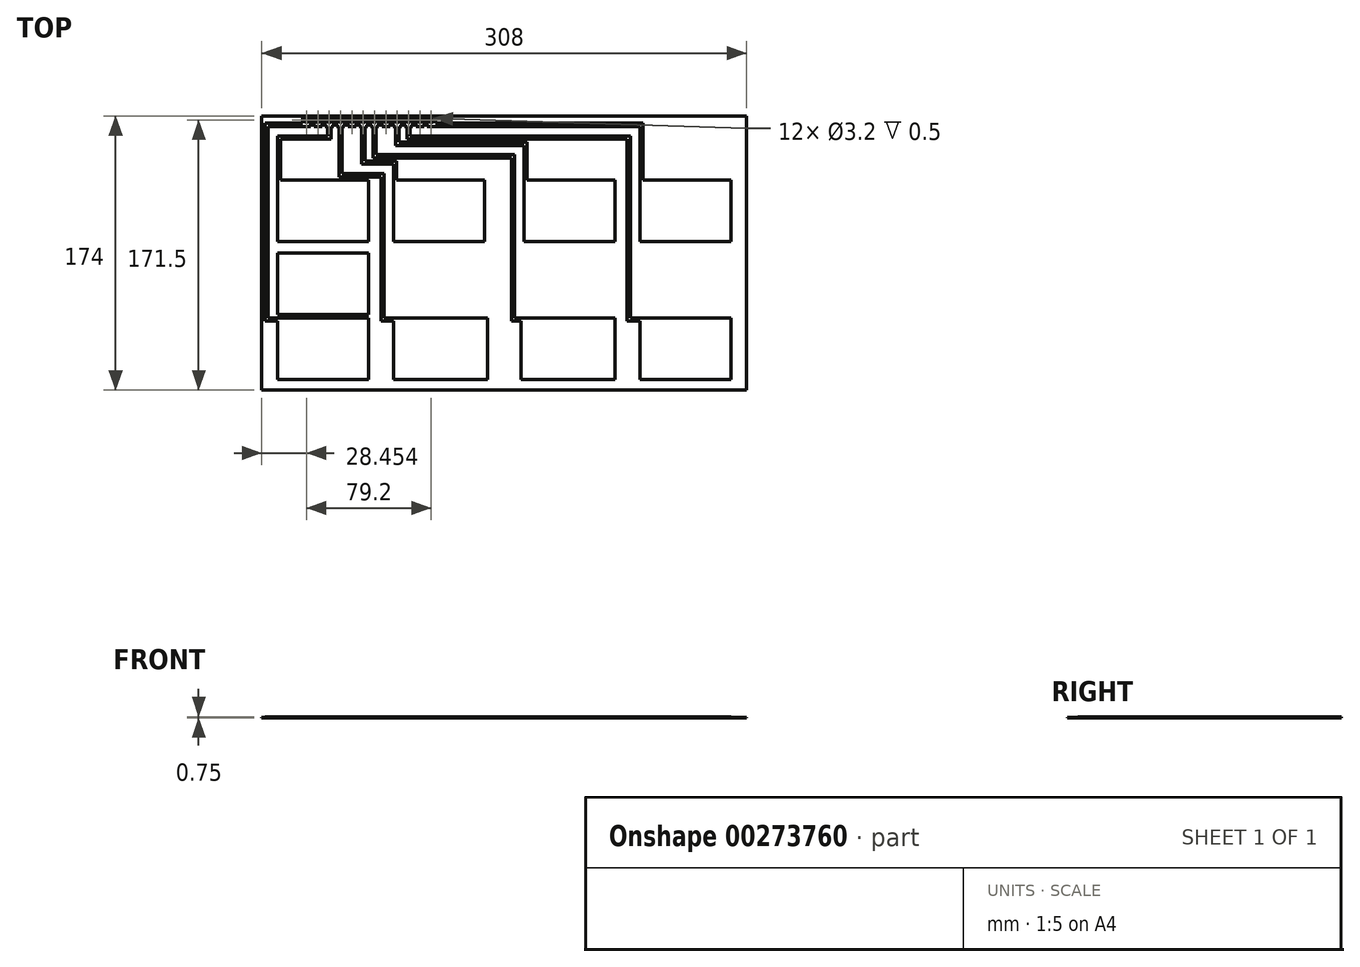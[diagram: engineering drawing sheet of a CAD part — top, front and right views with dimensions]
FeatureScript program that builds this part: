
annotation { "Feature Type Name" : "Feature", "Feature Type Description" : "" }
export const myFeature = defineFeature(function(context is Context, id is Id, definition is map)
    precondition{}
    {
        {
            var Q0;
            Q0=qCreatedBy(makeId("Top.planeOp"),FACE);
            var sketch = newSketch(context, id + "F0", { "sketchPlane" : qUnion([Q0])});
            skLineSegment(sketch, "E0.bottom", {"start": v(154, 87) * mm, "end": v(-154, 87) * mm});
            skLineSegment(sketch, "E0.top", {"start": v(154, -87) * mm, "end": v(-154, -87) * mm});
            skLineSegment(sketch, "E0.left", {"start": v(154, 87) * mm, "end": v(154, -87) * mm});
            skLineSegment(sketch, "E0.right", {"start": v(-154, 87) * mm, "end": v(-154, -87) * mm});
            skPoint(sketch, "E0.middle", {"position": v(0, 0) * mm});
            skSolve(sketch);
        }
        {
            var Q0;
            Q0=makeQuery(id+"F0.imprint","IMPRINT",FACE,{"disambiguationData":[TD([[makeQuery(id+"F0.imprint","IMPRINT",EDGE,{"derivedFrom":sQuery(id+"F0.wireOp",EDGE,"E0.bottom")}),1.0]])]});
            extrude(context, id + "F1", {"entities" : qUnion([Q0]), "depth" : .25 * mm});
        }
        {
            var Q0;
            Q0=makeQuery(id+"F1.opExtrude","CAP_FACE",FACE,{"disambiguationData":[OSD([sQuery(id+"F0.wireOp",EDGE,"E0.bottom"),sQuery(id+"F0.wireOp",EDGE,"E0.top"),sQuery(id+"F0.wireOp",EDGE,"E0.left"),sQuery(id+"F0.wireOp",EDGE,"E0.right")])],"isStart":false});
            var sketch = newSketch(context, id + "F2", { "sketchPlane" : qUnion([Q0])});
            skLineSegment(sketch, "E1", {"start": v(-85.95, 87) * mm, "end": v(-85.95, 80.4) * mm, "construction": true});
            skCircle(sketch, "E2", {"center": v(-89.55, 84.5) * mm, "radius": 1.6 * mm});
            skLineSegment(sketch, "E3", {"start": v(-89.55, 84.5) * mm, "end": v(-89.55, 80.4) * mm, "construction": true});
            skPoint(sketch, "E4", {"position": v(0, 80.62) * mm});
            skLineSegment(sketch, "E5.direction1", {"start": v(-89.55, 84.5) * mm, "end": v(-82.35, 84.5) * mm, "construction": true});
            skLineSegment(sketch, "E6", {"start": v(-86.95, 87) * mm, "end": v(-86.95, 80.4) * mm});
            skLineSegment(sketch, "E7.MirrorCS", {"start": v(-92.15, 87) * mm, "end": v(-92.15, 80.4) * mm});
            skLineSegment(sketch, "E8.trimOffspring", {"start": v(-92.15, 80.4) * mm, "end": v(-86.95, 80.4) * mm});
            skLineSegment(sketch, "E9.trimOffspring", {"start": v(-92.15, 87) * mm, "end": v(-86.95, 87) * mm});
            skCircle(sketch, "E10.1.0.0", {"center": v(-96.75, 84.5) * mm, "radius": 1.6 * mm});
            skLineSegment(sketch, "E10.1.0.1", {"start": v(-99.35, 87) * mm, "end": v(-99.35, 80.4) * mm});
            skLineSegment(sketch, "E10.1.0.2", {"start": v(-99.35, 87) * mm, "end": v(-94.15, 87) * mm});
            skLineSegment(sketch, "E10.1.0.3", {"start": v(-94.15, 87) * mm, "end": v(-94.15, 80.4) * mm});
            skLineSegment(sketch, "E10.1.0.4", {"start": v(-99.35, 80.4) * mm, "end": v(-94.15, 80.4) * mm});
            skCircle(sketch, "E10.2.0.0", {"center": v(-103.95, 84.5) * mm, "radius": 1.6 * mm});
            skLineSegment(sketch, "E10.2.0.1", {"start": v(-106.55, 87) * mm, "end": v(-106.55, 80.4) * mm});
            skLineSegment(sketch, "E10.2.0.2", {"start": v(-106.55, 87) * mm, "end": v(-101.35, 87) * mm});
            skLineSegment(sketch, "E10.2.0.3", {"start": v(-101.35, 87) * mm, "end": v(-101.35, 80.4) * mm});
            skLineSegment(sketch, "E10.2.0.4", {"start": v(-106.55, 80.4) * mm, "end": v(-101.35, 80.4) * mm});
            skCircle(sketch, "E10.3.0.0", {"center": v(-111.15, 84.5) * mm, "radius": 1.6 * mm});
            skLineSegment(sketch, "E10.3.0.1", {"start": v(-113.75, 87) * mm, "end": v(-113.75, 80.4) * mm});
            skLineSegment(sketch, "E10.3.0.2", {"start": v(-113.75, 87) * mm, "end": v(-108.55, 87) * mm});
            skLineSegment(sketch, "E10.3.0.3", {"start": v(-108.55, 87) * mm, "end": v(-108.55, 80.4) * mm});
            skLineSegment(sketch, "E10.3.0.4", {"start": v(-113.75, 80.4) * mm, "end": v(-108.55, 80.4) * mm});
            skCircle(sketch, "E10.4.0.0", {"center": v(-118.35, 84.5) * mm, "radius": 1.6 * mm});
            skLineSegment(sketch, "E10.4.0.1", {"start": v(-120.95, 87) * mm, "end": v(-120.95, 80.4) * mm});
            skLineSegment(sketch, "E10.4.0.2", {"start": v(-120.95, 87) * mm, "end": v(-115.75, 87) * mm});
            skLineSegment(sketch, "E10.4.0.3", {"start": v(-115.75, 87) * mm, "end": v(-115.75, 80.4) * mm});
            skLineSegment(sketch, "E10.4.0.4", {"start": v(-120.95, 80.4) * mm, "end": v(-115.75, 80.4) * mm});
            skCircle(sketch, "E10.5.0.0", {"center": v(-125.55, 84.5) * mm, "radius": 1.6 * mm});
            skLineSegment(sketch, "E10.5.0.1", {"start": v(-128.15, 87) * mm, "end": v(-128.15, 80.4) * mm});
            skLineSegment(sketch, "E10.5.0.2", {"start": v(-128.15, 87) * mm, "end": v(-122.95, 87) * mm});
            skLineSegment(sketch, "E10.5.0.3", {"start": v(-122.95, 87) * mm, "end": v(-122.95, 80.4) * mm});
            skLineSegment(sketch, "E10.5.0.4", {"start": v(-128.15, 80.4) * mm, "end": v(-122.95, 80.4) * mm});
            skLineSegment(sketch, "E10.direction1", {"start": v(-89.55, 84.5) * mm, "end": v(-96.75, 84.5) * mm, "construction": true});
            skCircle(sketch, "E11.MirrorC", {"center": v(-82.35, 84.5) * mm, "radius": 1.6 * mm});
            skLineSegment(sketch, "E12.MirrorCS", {"start": v(-79.75, 80.4) * mm, "end": v(-84.95, 80.4) * mm});
            skLineSegment(sketch, "E13.MirrorCS", {"start": v(-84.95, 87) * mm, "end": v(-84.95, 80.4) * mm});
            skLineSegment(sketch, "E14.MirrorCS", {"start": v(-79.75, 87) * mm, "end": v(-84.95, 87) * mm});
            skLineSegment(sketch, "E15.MirrorCS", {"start": v(-79.75, 87) * mm, "end": v(-79.75, 80.4) * mm});
            skLineSegment(sketch, "E16.MirrorCS", {"start": v(-77.75, 87) * mm, "end": v(-77.75, 80.4) * mm});
            skCircle(sketch, "E17.MirrorC", {"center": v(-75.15, 84.5) * mm, "radius": 1.6 * mm});
            skLineSegment(sketch, "E18.MirrorCS", {"start": v(-72.55, 87) * mm, "end": v(-77.75, 87) * mm});
            skLineSegment(sketch, "E19.MirrorCS", {"start": v(-72.55, 87) * mm, "end": v(-72.55, 80.4) * mm});
            skLineSegment(sketch, "E20.MirrorCS", {"start": v(-70.55, 87) * mm, "end": v(-70.55, 80.4) * mm});
            skCircle(sketch, "E21.MirrorC", {"center": v(-67.95, 84.5) * mm, "radius": 1.6 * mm});
            skLineSegment(sketch, "E22.MirrorCS", {"start": v(-65.35, 87) * mm, "end": v(-65.35, 80.4) * mm});
            skLineSegment(sketch, "E23.MirrorCS", {"start": v(-65.35, 87) * mm, "end": v(-70.55, 87) * mm});
            skLineSegment(sketch, "E24.MirrorCS", {"start": v(-63.35, 87) * mm, "end": v(-63.35, 80.4) * mm});
            skLineSegment(sketch, "E25.MirrorCS", {"start": v(-58.15, 87) * mm, "end": v(-63.35, 87) * mm});
            skCircle(sketch, "E26.MirrorC", {"center": v(-60.75, 84.5) * mm, "radius": 1.6 * mm});
            skLineSegment(sketch, "E27.MirrorCS", {"start": v(-58.15, 87) * mm, "end": v(-58.15, 80.4) * mm});
            skLineSegment(sketch, "E28.MirrorCS", {"start": v(-58.15, 80.4) * mm, "end": v(-63.35, 80.4) * mm});
            skLineSegment(sketch, "E29.MirrorCS", {"start": v(-56.15, 87) * mm, "end": v(-56.15, 80.4) * mm});
            skLineSegment(sketch, "E30.MirrorCS", {"start": v(-50.95, 87) * mm, "end": v(-56.15, 87) * mm});
            skLineSegment(sketch, "E31.MirrorCS", {"start": v(-50.95, 87) * mm, "end": v(-50.95, 80.4) * mm});
            skCircle(sketch, "E32.MirrorC", {"center": v(-53.55, 84.5) * mm, "radius": 1.6 * mm});
            skLineSegment(sketch, "E33.MirrorCS", {"start": v(-48.95, 87) * mm, "end": v(-48.95, 80.4) * mm});
            skCircle(sketch, "E34.MirrorC", {"center": v(-46.35, 84.5) * mm, "radius": 1.6 * mm});
            skLineSegment(sketch, "E35.MirrorCS", {"start": v(-43.75, 87) * mm, "end": v(-48.95, 87) * mm});
            skLineSegment(sketch, "E36.MirrorCS", {"start": v(-43.75, 87) * mm, "end": v(-43.75, 80.4) * mm});
            skLineSegment(sketch, "E37.left", {"start": v(-86.11, 46.4) * mm, "end": v(-86.11, 7.22) * mm});
            skLineSegment(sketch, "E38", {"start": v(0, 87) * mm, "end": v(0, -87) * mm, "construction": true});
            skLineSegment(sketch, "E39.bottom", {"start": v(-70.38, 46.4) * mm, "end": v(-12.5, 46.4) * mm});
            skLineSegment(sketch, "E39.top", {"start": v(-70.38, 7.22) * mm, "end": v(-12.5, 7.22) * mm});
            skLineSegment(sketch, "E39.left", {"start": v(-70.38, 46.4) * mm, "end": v(-70.38, 7.22) * mm});
            skLineSegment(sketch, "E39.right", {"start": v(-12.5, 46.4) * mm, "end": v(-12.5, 7.22) * mm});
            skLineSegment(sketch, "E40.bottom", {"start": v(-144, 7.22) * mm, "end": v(-86.11, 7.22) * mm});
            skLineSegment(sketch, "E40.left", {"start": v(-144, 0) * mm, "end": v(-144, -39.18) * mm});
            skLineSegment(sketch, "E41.left", {"start": v(-144, -41.18) * mm, "end": v(-144, -80.36) * mm});
            skLineSegment(sketch, "E41.right", {"start": v(-86.11, -41.18) * mm, "end": v(-86.11, -80.36) * mm});
            skLineSegment(sketch, "E42.top", {"start": v(-70.38, -37.1) * mm, "end": v(-10.64, -37.1) * mm});
            skLineSegment(sketch, "E42.left", {"start": v(-70.38, 0) * mm, "end": v(-70.38, -37.1) * mm});
            skLineSegment(sketch, "E43.bottom", {"start": v(-70.38, -41.18) * mm, "end": v(-10.64, -41.18) * mm});
            skLineSegment(sketch, "E43.top", {"start": v(-70.38, -80.36) * mm, "end": v(-10.64, -80.36) * mm});
            skLineSegment(sketch, "E43.left", {"start": v(-70.38, -41.18) * mm, "end": v(-70.38, -80.36) * mm});
            skLineSegment(sketch, "E43.right", {"start": v(-10.64, -41.18) * mm, "end": v(-10.64, -80.36) * mm});
            skLineSegment(sketch, "E44", {"start": v(-144, 87) * mm, "end": v(-154, 87) * mm, "construction": true});
            skLineSegment(sketch, "E45", {"start": v(-36.86, -77) * mm, "end": v(-36.86, -87) * mm, "construction": true});
            skLineSegment(sketch, "E46", {"start": v(-144, -39.18) * mm, "end": v(-144, -41.18) * mm, "construction": true});
            skLineSegment(sketch, "E47", {"start": v(-70.38, 7.22) * mm, "end": v(-70.38, 0) * mm, "construction": true});
            skLineSegment(sketch, "E48", {"start": v(-70.38, -37.1) * mm, "end": v(-70.38, -41.18) * mm, "construction": true});
            skLineSegment(sketch, "E49", {"start": v(-86.11, -39.18) * mm, "end": v(-144, -39.18) * mm});
            skLineSegment(sketch, "E50", {"start": v(-144, -41.18) * mm, "end": v(-86.11, -41.18) * mm});
            skLineSegment(sketch, "E51", {"start": v(-86.11, 46.4) * mm, "end": v(-70.38, 46.4) * mm, "construction": true});
            skLineSegment(sketch, "E52", {"start": v(-150, 80.4) * mm, "end": v(-150, -41.18) * mm});
            skPoint(sketch, "E53", {"position": v(-125.55, 80.4) * mm});
            skPoint(sketch, "E54", {"position": v(-118.35, 80.4) * mm});
            skPoint(sketch, "E55", {"position": v(-111.15, 80.4) * mm});
            skLineSegment(sketch, "E56", {"start": v(-117.35, 80.4) * mm, "end": v(-117.35, 76.4) * mm});
            skLineSegment(sketch, "E57", {"start": v(-117.35, 76.4) * mm, "end": v(-146, 76.4) * mm});
            skLineSegment(sketch, "E58", {"start": v(-146, 76.4) * mm, "end": v(-146, 3.97) * mm});
            skLineSegment(sketch, "E59", {"start": v(-110.15, 80.4) * mm, "end": v(-110.15, 72.4) * mm});
            skLineSegment(sketch, "E60", {"start": v(-146, 3.97) * mm, "end": v(-144.5, 3.97) * mm});
            skLineSegment(sketch, "E61", {"start": v(-144, -41.18) * mm, "end": v(-150, -41.18) * mm});
            skLineSegment(sketch, "E62.0", {"start": v(-148, 1.97) * mm, "end": v(-144, 1.97) * mm});
            skLineSegment(sketch, "E62.1", {"start": v(-148, 78.4) * mm, "end": v(-148, 1.97) * mm});
            skLineSegment(sketch, "E62.2", {"start": v(-119.35, 78.4) * mm, "end": v(-148, 78.4) * mm});
            skLineSegment(sketch, "E62.3", {"start": v(-119.35, 80.4) * mm, "end": v(-119.35, 78.4) * mm});
            skLineSegment(sketch, "E63.0", {"start": v(-144, -43.18) * mm, "end": v(-152, -43.18) * mm});
            skLineSegment(sketch, "E63.1", {"start": v(-152, 82.4) * mm, "end": v(-152, -43.18) * mm});
            skPoint(sketch, "E64", {"position": v(-103.95, 80.4) * mm});
            skPoint(sketch, "E65", {"position": v(-96.75, 80.4) * mm});
            skPoint(sketch, "E66", {"position": v(-82.35, 80.4) * mm});
            skPoint(sketch, "E67", {"position": v(-75.15, 80.4) * mm});
            skLineSegment(sketch, "E68", {"start": v(-102.95, 80.4) * mm, "end": v(-102.95, 50.4) * mm});
            skLineSegment(sketch, "E69", {"start": v(-102.95, 50.4) * mm, "end": v(-76.38, 50.4) * mm});
            skLineSegment(sketch, "E70", {"start": v(-76.38, 50.4) * mm, "end": v(-76.38, -41.18) * mm});
            skLineSegment(sketch, "E71", {"start": v(-76.38, -41.18) * mm, "end": v(-70.38, -41.18) * mm});
            skLineSegment(sketch, "E72", {"start": v(-95.75, 80.4) * mm, "end": v(-95.75, 54.4) * mm});
            skLineSegment(sketch, "E73", {"start": v(-95.75, 54.4) * mm, "end": v(-72.38, 54.4) * mm});
            skLineSegment(sketch, "E74", {"start": v(-72.38, 54.4) * mm, "end": v(-72.38, 0) * mm});
            skLineSegment(sketch, "E75.0", {"start": v(-78.38, -43.18) * mm, "end": v(-70.38, -43.18) * mm});
            skLineSegment(sketch, "E75.1", {"start": v(-78.38, 48.4) * mm, "end": v(-78.38, -43.18) * mm});
            skLineSegment(sketch, "E75.2", {"start": v(-104.95, 48.4) * mm, "end": v(-78.38, 48.4) * mm});
            skLineSegment(sketch, "E75.3", {"start": v(-104.95, 80.4) * mm, "end": v(-104.95, 48.4) * mm});
            skLineSegment(sketch, "E76.0", {"start": v(-74.38, -2) * mm, "end": v(-70.38, -2) * mm});
            skLineSegment(sketch, "E76.1", {"start": v(-74.38, 52.4) * mm, "end": v(-74.38, -2) * mm});
            skLineSegment(sketch, "E76.2", {"start": v(-97.75, 52.4) * mm, "end": v(-74.38, 52.4) * mm});
            skLineSegment(sketch, "E76.3", {"start": v(-97.75, 80.4) * mm, "end": v(-97.75, 52.4) * mm});
            skLineSegment(sketch, "E77", {"start": v(-86.11, -41.18) * mm, "end": v(-76.38, -41.18) * mm, "construction": true});
            skLineSegment(sketch, "E78", {"start": v(-88.55, 80.4) * mm, "end": v(-88.55, 58.4) * mm});
            skLineSegment(sketch, "E79", {"start": v(-88.55, 58.4) * mm, "end": v(-68.38, 58.4) * mm});
            skLineSegment(sketch, "E80", {"start": v(-68.38, 58.4) * mm, "end": v(-68.38, 46.4) * mm});
            skLineSegment(sketch, "E81", {"start": v(-81.35, 80.4) * mm, "end": v(-81.35, 62.4) * mm});
            skLineSegment(sketch, "E82", {"start": v(-144, 46.4) * mm, "end": v(-144, 7.22) * mm});
            skLineSegment(sketch, "E83.MirrorCS", {"start": v(12.5, 46.4) * mm, "end": v(12.5, 7.22) * mm});
            skLineSegment(sketch, "E84.MirrorCS", {"start": v(70.38, 46.4) * mm, "end": v(12.5, 46.4) * mm});
            skLineSegment(sketch, "E85.MirrorCS", {"start": v(70.38, 46.4) * mm, "end": v(70.38, 7.22) * mm});
            skLineSegment(sketch, "E86.MirrorCS", {"start": v(70.38, 7.22) * mm, "end": v(12.5, 7.22) * mm});
            skLineSegment(sketch, "E87.MirrorCS", {"start": v(86.11, 46.4) * mm, "end": v(86.11, 7.22) * mm});
            skLineSegment(sketch, "E88.MirrorCS", {"start": v(86.11, 46.4) * mm, "end": v(144, 46.4) * mm});
            skLineSegment(sketch, "E89.MirrorCS", {"start": v(144, 46.4) * mm, "end": v(144, 7.22) * mm});
            skLineSegment(sketch, "E90.MirrorCS", {"start": v(144, 7.22) * mm, "end": v(86.11, 7.22) * mm});
            skLineSegment(sketch, "E91.MirrorCS", {"start": v(144, 0) * mm, "end": v(144, -39.18) * mm});
            skLineSegment(sketch, "E92.MirrorCS", {"start": v(86.11, 0) * mm, "end": v(86.11, -39.18) * mm});
            skLineSegment(sketch, "E93.MirrorCS", {"start": v(144, -41.18) * mm, "end": v(86.11, -41.18) * mm});
            skLineSegment(sketch, "E94.MirrorCS", {"start": v(86.11, -41.18) * mm, "end": v(86.11, -80.36) * mm});
            skLineSegment(sketch, "E95.MirrorCS", {"start": v(70.38, -41.18) * mm, "end": v(70.38, -80.36) * mm});
            skLineSegment(sketch, "E96.MirrorCS", {"start": v(10.64, -41.18) * mm, "end": v(10.64, -80.36) * mm});
            skLineSegment(sketch, "E97.MirrorCS", {"start": v(70.38, -41.18) * mm, "end": v(10.64, -41.18) * mm});
            skLineSegment(sketch, "E98.MirrorCS", {"start": v(70.38, -37.1) * mm, "end": v(10.64, -37.1) * mm});
            skLineSegment(sketch, "E99.MirrorCS", {"start": v(11.39, 0) * mm, "end": v(10.64, -37.1) * mm});
            skLineSegment(sketch, "E100.MirrorCS", {"start": v(70.38, 0) * mm, "end": v(70.38, -37.1) * mm});
            skLineSegment(sketch, "E101.MirrorCS", {"start": v(86.11, -39.18) * mm, "end": v(144, -39.18) * mm});
            skLineSegment(sketch, "E102", {"start": v(10.64, -80.36) * mm, "end": v(70.38, -80.36) * mm});
            skLineSegment(sketch, "E103", {"start": v(6.5, 62.4) * mm, "end": v(6.5, -41.18) * mm});
            skLineSegment(sketch, "E104", {"start": v(-81.35, 62.4) * mm, "end": v(6.5, 62.4) * mm});
            skLineSegment(sketch, "E105", {"start": v(10.64, -41.18) * mm, "end": v(6.5, -41.18) * mm});
            skLineSegment(sketch, "E106.0", {"start": v(-70.38, 56.4) * mm, "end": v(-70.38, 46.4) * mm});
            skLineSegment(sketch, "E106.1", {"start": v(-90.55, 56.4) * mm, "end": v(-70.38, 56.4) * mm});
            skLineSegment(sketch, "E106.2", {"start": v(-90.55, 80.4) * mm, "end": v(-90.55, 56.4) * mm});
            skLineSegment(sketch, "E107.0", {"start": v(10.64, -43.18) * mm, "end": v(4.5, -43.18) * mm});
            skLineSegment(sketch, "E107.1", {"start": v(4.5, 60.4) * mm, "end": v(4.5, -43.18) * mm});
            skLineSegment(sketch, "E107.2", {"start": v(-83.35, 60.4) * mm, "end": v(4.5, 60.4) * mm});
            skLineSegment(sketch, "E107.3", {"start": v(-83.35, 80.4) * mm, "end": v(-83.35, 60.4) * mm});
            skLineSegment(sketch, "E108", {"start": v(-74.15, 80.4) * mm, "end": v(-74.15, 66.4) * mm});
            skLineSegment(sketch, "E109", {"start": v(-74.15, 66.4) * mm, "end": v(10.5, 66.4) * mm});
            skLineSegment(sketch, "E110", {"start": v(10.5, 66.4) * mm, "end": v(10.5, 0) * mm});
            skLineSegment(sketch, "E111.0", {"start": v(8.5, -2) * mm, "end": v(11.35, -2) * mm});
            skLineSegment(sketch, "E111.1", {"start": v(8.5, 64.4) * mm, "end": v(8.5, -2) * mm});
            skLineSegment(sketch, "E111.2", {"start": v(-76.15, 64.4) * mm, "end": v(8.5, 64.4) * mm});
            skLineSegment(sketch, "E111.3", {"start": v(-76.15, 80.4) * mm, "end": v(-76.15, 64.4) * mm});
            skLineSegment(sketch, "E112", {"start": v(-66.95, 80.4) * mm, "end": v(-66.95, 70.4) * mm});
            skLineSegment(sketch, "E113", {"start": v(-66.95, 70.4) * mm, "end": v(14.5, 70.4) * mm});
            skLineSegment(sketch, "E114", {"start": v(14.5, 70.4) * mm, "end": v(14.5, 46.4) * mm});
            skLineSegment(sketch, "E115.0", {"start": v(12.5, 68.4) * mm, "end": v(12.5, 46.4) * mm});
            skLineSegment(sketch, "E115.1", {"start": v(-68.95, 68.4) * mm, "end": v(12.5, 68.4) * mm});
            skLineSegment(sketch, "E115.2", {"start": v(-68.95, 80.4) * mm, "end": v(-68.95, 68.4) * mm});
            skLineSegment(sketch, "E116", {"start": v(-59.75, 80.4) * mm, "end": v(-59.75, 74.4) * mm});
            skLineSegment(sketch, "E117", {"start": v(-59.75, 74.4) * mm, "end": v(80.11, 74.4) * mm});
            skLineSegment(sketch, "E118", {"start": v(80.11, 74.4) * mm, "end": v(80.11, -41.18) * mm});
            skLineSegment(sketch, "E119", {"start": v(80.11, -41.18) * mm, "end": v(86.11, -41.18) * mm});
            skLineSegment(sketch, "E120.2", {"start": v(-61.75, 72.4) * mm, "end": v(78.11, 72.4) * mm});
            skLineSegment(sketch, "E120.3", {"start": v(-61.75, 80.4) * mm, "end": v(-61.75, 72.4) * mm});
            skLineSegment(sketch, "E121", {"start": v(84.11, 78.4) * mm, "end": v(84.11, 0) * mm});
            skLineSegment(sketch, "E122.0", {"start": v(82.11, -2) * mm, "end": v(86.11, -2) * mm});
            skLineSegment(sketch, "E122.1", {"start": v(82.11, 76.4) * mm, "end": v(82.11, -2) * mm});
            skLineSegment(sketch, "E122.2", {"start": v(-54.55, 76.4) * mm, "end": v(82.11, 76.4) * mm});
            skLineSegment(sketch, "E122.3", {"start": v(-54.55, 80.4) * mm, "end": v(-54.55, 76.4) * mm});
            skLineSegment(sketch, "E123", {"start": v(-43.75, 82.4) * mm, "end": v(88.11, 82.4) * mm});
            skLineSegment(sketch, "E124", {"start": v(88.11, 82.4) * mm, "end": v(88.11, 46.4) * mm});
            skLineSegment(sketch, "E125.0", {"start": v(86.11, 80.4) * mm, "end": v(86.11, 46.4) * mm});
            skLineSegment(sketch, "E125.1", {"start": v(-43.75, 80.4) * mm, "end": v(86.11, 80.4) * mm});
            skLineSegment(sketch, "E126", {"start": v(-144, 46.4) * mm, "end": v(-86.11, 46.4) * mm});
            skLineSegment(sketch, "E127", {"start": v(-112.15, 80.4) * mm, "end": v(-112.15, 74.4) * mm});
            skLineSegment(sketch, "E128", {"start": v(-112.15, 74.4) * mm, "end": v(-144, 74.4) * mm});
            skLineSegment(sketch, "E129", {"start": v(-144, 74.4) * mm, "end": v(-144, 46.4) * mm});
            skLineSegment(sketch, "E130.0", {"start": v(-142, 72.4) * mm, "end": v(-142, 46.4) * mm});
            skLineSegment(sketch, "E130.1", {"start": v(-110.15, 72.4) * mm, "end": v(-142, 72.4) * mm});
            skLineSegment(sketch, "E131", {"start": v(78.11, 72.4) * mm, "end": v(78.11, -43.18) * mm});
            skLineSegment(sketch, "E132", {"start": v(78.11, -43.18) * mm, "end": v(86.11, -43.18) * mm});
            skLineSegment(sketch, "E133", {"start": v(-56.15, 80.4) * mm, "end": v(-50.95, 80.4) * mm});
            skPoint(sketch, "E134", {"position": v(-53.55, 80.4) * mm});
            skLineSegment(sketch, "E135", {"start": v(-70.55, 80.4) * mm, "end": v(-65.35, 80.4) * mm});
            skPoint(sketch, "E136", {"position": v(-67.95, 80.4) * mm});
            skLineSegment(sketch, "E137", {"start": v(-67.95, 84.5) * mm, "end": v(-67.95, 80.4) * mm, "construction": true});
            skLineSegment(sketch, "E138", {"start": v(-60.75, 84.5) * mm, "end": v(-60.75, 80.4) * mm, "construction": true});
            skLineSegment(sketch, "E139", {"start": v(-52.55, 80.4) * mm, "end": v(-52.55, 78.4) * mm});
            skLineSegment(sketch, "E140", {"start": v(-52.55, 78.4) * mm, "end": v(84.11, 78.4) * mm});
            skLineSegment(sketch, "E141", {"start": v(-77.75, 80.4) * mm, "end": v(-72.55, 80.4) * mm});
            skLineSegment(sketch, "E142", {"start": v(-48.95, 80.4) * mm, "end": v(-43.75, 80.4) * mm});
            skLineSegment(sketch, "E143", {"start": v(-46.35, 84.5) * mm, "end": v(-46.35, 80.4) * mm, "construction": true});
            skLineSegment(sketch, "E144", {"start": v(-144, -80.36) * mm, "end": v(-86.11, -80.36) * mm});
            skLineSegment(sketch, "E145", {"start": v(86.11, -80.36) * mm, "end": v(144.09, -80.36) * mm});
            skPoint(sketch, "E146.MirrorCS.start.orphan", {"position": v(144, -41.18) * mm});
            skLineSegment(sketch, "E147", {"start": v(144, -41.18) * mm, "end": v(144.09, -80.36) * mm});
            skLineSegment(sketch, "E148", {"start": v(-128.15, 80.4) * mm, "end": v(-150, 80.4) * mm});
            skLineSegment(sketch, "E149", {"start": v(-128.15, 82.4) * mm, "end": v(-152, 82.4) * mm});
            skLineSegment(sketch, "E150", {"start": v(-86.11, -39.18) * mm, "end": v(-86.11, 0) * mm});
            skLineSegment(sketch, "E151", {"start": v(-144, 0) * mm, "end": v(-86.11, 0) * mm});
            skSolve(sketch);
        }
        {
            var Q0;
            Q0=qSketchRegion(id+"F2",true);
            extrude(context, id + "F3", {"entities" : qUnion([Q0]), "operationType" : NewBodyOperationType.ADD, "depth" : .5 * mm});
        }
    });
